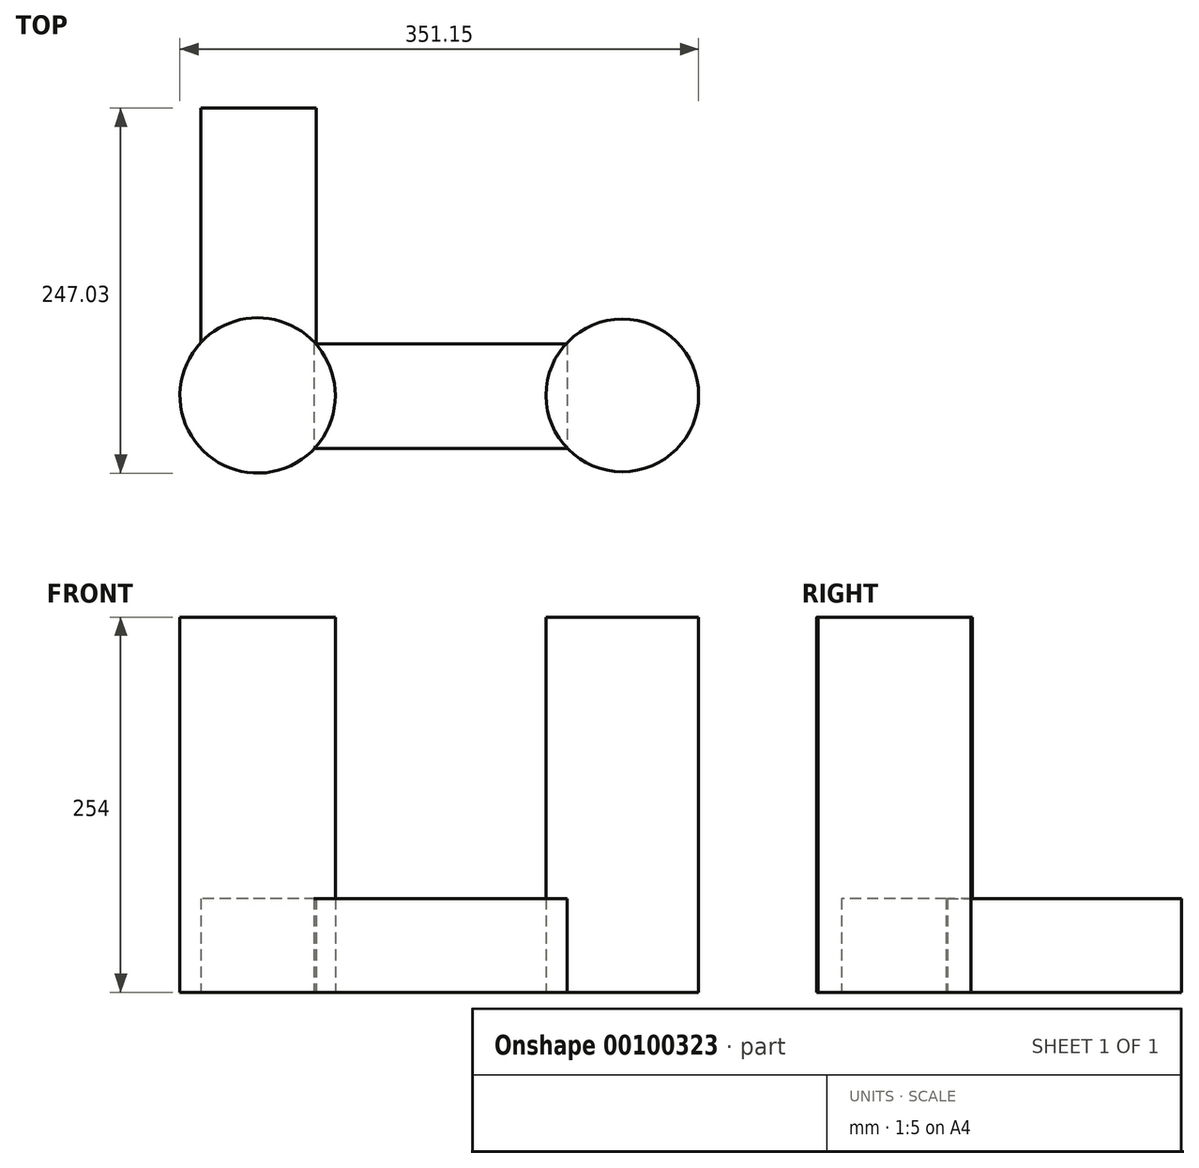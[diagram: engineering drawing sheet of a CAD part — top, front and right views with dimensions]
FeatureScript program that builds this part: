
annotation { "Feature Type Name" : "Feature", "Feature Type Description" : "" }
export const myFeature = defineFeature(function(context is Context, id is Id, definition is map)
    precondition{}
    {
        {
            var Q0;
            Q0=qCreatedBy(makeId("Top.planeOp"),FACE);
            var sketch = newSketch(context, id + "F0", { "sketchPlane" : qUnion([Q0])});
            skCircle(sketch, "E0", {"center": v(0, 0) * mm, "radius": 52.58 * mm});
            skSolve(sketch);
        }
        {
            var Q0;
            Q0=makeQuery(id+"F0.imprint","IMPRINT",FACE,{"disambiguationData":[TD([[makeQuery(id+"F0.imprint","IMPRINT",EDGE,{"derivedFrom":sQuery(id+"F0.wireOp",EDGE,"E0")}),1.0]])]});
            extrude(context, id + "F1", {"entities" : qUnion([Q0]), "depth" : 254 * mm});
        }
        {
            var Q0;
            Q0=qCreatedBy(makeId("Top.planeOp"),FACE);
            var sketch = newSketch(context, id + "F2", { "sketchPlane" : qUnion([Q0])});
            skCircle(sketch, "E1", {"center": v(246.88, 0) * mm, "radius": 51.69 * mm});
            skSolve(sketch);
        }
        {
            var Q0;
            Q0=makeQuery(id+"F2.imprint","IMPRINT",FACE,{"disambiguationData":[TD([[makeQuery(id+"F2.imprint","IMPRINT",EDGE,{"derivedFrom":sQuery(id+"F2.wireOp",EDGE,"E1")}),1.0]])]});
            extrude(context, id + "F3", {"entities" : qUnion([Q0]), "operationType" : NewBodyOperationType.ADD, "depth" : 254 * mm});
        }
        {
            var Q0;
            Q0=qCreatedBy(makeId("Top.planeOp"),FACE);
            var sketch = newSketch(context, id + "F4", { "sketchPlane" : qUnion([Q0])});
            skLineSegment(sketch, "E2.bottom", {"start": v(38.03, 34.98) * mm, "end": v(209.37, 34.98) * mm});
            skLineSegment(sketch, "E2.top", {"start": v(38.03, -36.02) * mm, "end": v(209.37, -36.02) * mm});
            skLineSegment(sketch, "E2.left", {"start": v(38.03, 34.98) * mm, "end": v(38.03, -36.02) * mm});
            skLineSegment(sketch, "E2.right", {"start": v(209.37, 34.98) * mm, "end": v(209.37, -36.02) * mm});
            skSolve(sketch);
        }
        {
            var Q0;
            Q0=makeQuery(id+"F4.imprint","IMPRINT",FACE,{"disambiguationData":[TD([[makeQuery(id+"F4.imprint","IMPRINT",EDGE,{"derivedFrom":sQuery(id+"F4.wireOp",EDGE,"E2.bottom")}),-1.0]])]});
            extrude(context, id + "F5", {"entities" : qUnion([Q0]), "depth" : 63.5 * mm});
        }
        {
            var Q0;
            Q0=qCreatedBy(makeId("Top.planeOp"),FACE);
            var sketch = newSketch(context, id + "F6", { "sketchPlane" : qUnion([Q0])});
            skLineSegment(sketch, "E3.bottom", {"start": v(39.52, 35.03) * mm, "end": v(-38.58, 35.03) * mm});
            skLineSegment(sketch, "E3.top", {"start": v(39.52, 194.45) * mm, "end": v(-38.58, 194.45) * mm});
            skLineSegment(sketch, "E3.left", {"start": v(39.52, 35.03) * mm, "end": v(39.52, 194.45) * mm});
            skLineSegment(sketch, "E3.right", {"start": v(-38.58, 35.03) * mm, "end": v(-38.58, 194.45) * mm});
            skSolve(sketch);
        }
        {
            var Q0;
            Q0=makeQuery(id+"F6.imprint","IMPRINT",FACE,{"disambiguationData":[TD([[makeQuery(id+"F6.imprint","IMPRINT",EDGE,{"derivedFrom":sQuery(id+"F6.wireOp",EDGE,"E3.bottom")}),-1.0]])]});
            extrude(context, id + "F7", {"entities" : qUnion([Q0]), "operationType" : NewBodyOperationType.ADD, "depth" : 63.5 * mm});
        }
    });
